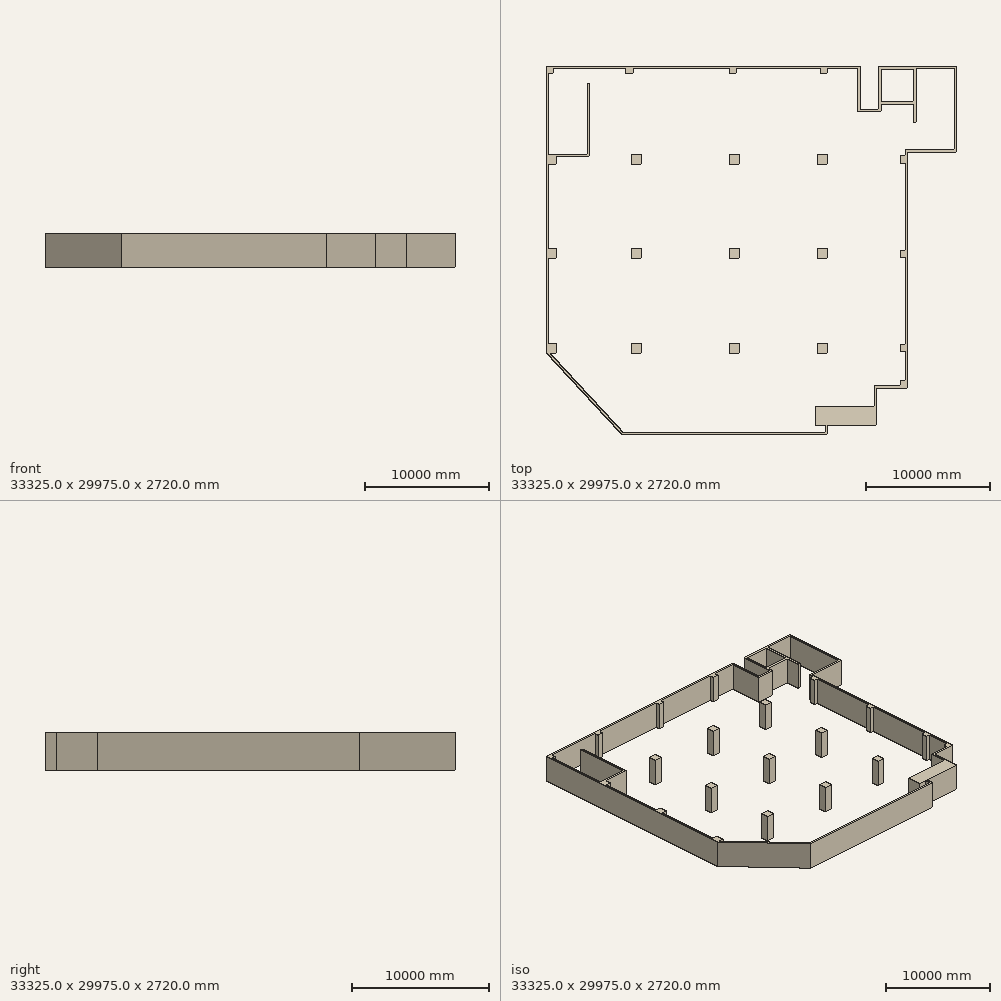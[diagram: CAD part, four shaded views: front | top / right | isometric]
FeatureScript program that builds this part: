
annotation { "Feature Type Name" : "Feature", "Feature Type Description" : "" }
export const myFeature = defineFeature(function(context is Context, id is Id, definition is map)
    precondition{}
    {
        {
            assignVariable(context, id + "F0", {"name" : "Wall_Height", "anyValue" : 2720});
        }
        {
            var Q0;
            Q0=qCreatedBy(makeId("Top.planeOp"),FACE);
            var sketch = newSketch(context, id + "F1", { "sketchPlane" : qUnion([Q0])});
            skLineSegment(sketch, "E0.bottom", {"start": v(0, 0) * mm, "end": v(33325, 0) * mm});
            skLineSegment(sketch, "E0.top", {"start": v(6150, -29975) * mm, "end": v(22850, -29975) * mm});
            skLineSegment(sketch, "E0.left", {"start": v(0, 0) * mm, "end": v(0, -23325) * mm});
            skLineSegment(sketch, "E0.right", {"start": v(33325, 0) * mm, "end": v(33325, -7000) * mm});
            skLineSegment(sketch, "E1", {"start": v(33325, -7000) * mm, "end": v(29350, -7000) * mm});
            skLineSegment(sketch, "E2", {"start": v(29350, -7000) * mm, "end": v(29350, -26190) * mm});
            skLineSegment(sketch, "E3", {"start": v(29350, -26190) * mm, "end": v(26850, -26190) * mm});
            skLineSegment(sketch, "E4", {"start": v(26850, -26190) * mm, "end": v(26850, -29190) * mm});
            skLineSegment(sketch, "E5", {"start": v(26850, -29190) * mm, "end": v(21850, -29190) * mm});
            skLineSegment(sketch, "E6", {"start": v(22850, -29190) * mm, "end": v(22850, -29975) * mm});
            skLineSegment(sketch, "E7", {"start": v(0, -23325) * mm, "end": v(6150, -29975) * mm});
            skLineSegment(sketch, "E8.1", {"start": v(22650, -29190) * mm, "end": v(22650, -29775) * mm});
            skLineSegment(sketch, "E8.2", {"start": v(6237.45, -29775) * mm, "end": v(22650, -29775) * mm});
            skLineSegment(sketch, "E8.3", {"start": v(200, -23246.7) * mm, "end": v(6237.45, -29775) * mm});
            skLineSegment(sketch, "E8.4", {"start": v(200, -600) * mm, "end": v(200, -7175) * mm});
            skLineSegment(sketch, "E8.5", {"start": v(26650, -25990) * mm, "end": v(26650, -27690) * mm});
            skLineSegment(sketch, "E8.6", {"start": v(28750, -25990) * mm, "end": v(26650, -25990) * mm});
            skLineSegment(sketch, "E8.7", {"start": v(29150, -6800) * mm, "end": v(29150, -7300) * mm});
            skLineSegment(sketch, "E8.8", {"start": v(33125, -6800) * mm, "end": v(29150, -6800) * mm});
            skLineSegment(sketch, "E8.9", {"start": v(33125, -200) * mm, "end": v(33125, -6800) * mm});
            skLineSegment(sketch, "E8.10", {"start": v(600, -200) * mm, "end": v(6450, -200) * mm});
            skLineSegment(sketch, "E9.bottom", {"start": v(600, -600) * mm, "end": v(0, -600) * mm});
            skLineSegment(sketch, "E9.left", {"start": v(600, -600) * mm, "end": v(600, 0) * mm});
            skLineSegment(sketch, "E10", {"start": v(7050, 0) * mm, "end": v(7050, -600) * mm});
            skLineSegment(sketch, "E11", {"start": v(6450, -600) * mm, "end": v(7050, -600) * mm});
            skLineSegment(sketch, "E12", {"start": v(6450, -600) * mm, "end": v(6450, 0) * mm});
            skLineSegment(sketch, "E13", {"start": v(14850, 0) * mm, "end": v(14850, -600) * mm});
            skLineSegment(sketch, "E14", {"start": v(14850, -600) * mm, "end": v(15450, -600) * mm});
            skLineSegment(sketch, "E15", {"start": v(15450, -600) * mm, "end": v(15450, 0) * mm});
            skLineSegment(sketch, "E16", {"start": v(22850, 0) * mm, "end": v(22850, -600) * mm});
            skLineSegment(sketch, "E17", {"start": v(22250, -600) * mm, "end": v(22850, -600) * mm});
            skLineSegment(sketch, "E18", {"start": v(22250, -600) * mm, "end": v(22250, 0) * mm});
            skLineSegment(sketch, "E19", {"start": v(0, -23325) * mm, "end": v(800, -23325) * mm});
            skLineSegment(sketch, "E20", {"start": v(800, -23325) * mm, "end": v(800, -22525) * mm});
            skLineSegment(sketch, "E21", {"start": v(800, -22525) * mm, "end": v(0, -22525) * mm});
            skLineSegment(sketch, "E22", {"start": v(0, -15625) * mm, "end": v(800, -15625) * mm});
            skLineSegment(sketch, "E23", {"start": v(800, -15625) * mm, "end": v(800, -14825) * mm});
            skLineSegment(sketch, "E24", {"start": v(800, -14825) * mm, "end": v(0, -14825) * mm});
            skLineSegment(sketch, "E25", {"start": v(0, -7975) * mm, "end": v(800, -7975) * mm});
            skLineSegment(sketch, "E26", {"start": v(800, -7975) * mm, "end": v(800, -7175) * mm});
            skLineSegment(sketch, "E27", {"start": v(800, -7175) * mm, "end": v(0, -7175) * mm});
            skLineSegment(sketch, "E28.bottom", {"start": v(6925, -7975) * mm, "end": v(7725, -7975) * mm});
            skLineSegment(sketch, "E28.top", {"start": v(6925, -7175) * mm, "end": v(7725, -7175) * mm});
            skLineSegment(sketch, "E28.left", {"start": v(6925, -7975) * mm, "end": v(6925, -7175) * mm});
            skLineSegment(sketch, "E28.right", {"start": v(7725, -7975) * mm, "end": v(7725, -7175) * mm});
            skLineSegment(sketch, "E29.bottom", {"start": v(6925, -15625) * mm, "end": v(7725, -15625) * mm});
            skLineSegment(sketch, "E29.top", {"start": v(6925, -14825) * mm, "end": v(7725, -14825) * mm});
            skLineSegment(sketch, "E29.left", {"start": v(6925, -15625) * mm, "end": v(6925, -14825) * mm});
            skLineSegment(sketch, "E29.right", {"start": v(7725, -15625) * mm, "end": v(7725, -14825) * mm});
            skLineSegment(sketch, "E30.bottom", {"start": v(6925, -23325) * mm, "end": v(7725, -23325) * mm});
            skLineSegment(sketch, "E30.top", {"start": v(6925, -22525) * mm, "end": v(7725, -22525) * mm});
            skLineSegment(sketch, "E30.left", {"start": v(6925, -23325) * mm, "end": v(6925, -22525) * mm});
            skLineSegment(sketch, "E30.right", {"start": v(7725, -23325) * mm, "end": v(7725, -22525) * mm});
            skLineSegment(sketch, "E31.1.0.0", {"start": v(15650, -15625) * mm, "end": v(15650, -14825) * mm});
            skLineSegment(sketch, "E31.1.0.1", {"start": v(14850, -23325) * mm, "end": v(15650, -23325) * mm});
            skLineSegment(sketch, "E31.1.0.2", {"start": v(14850, -15625) * mm, "end": v(14850, -14825) * mm});
            skLineSegment(sketch, "E31.1.0.3", {"start": v(14850, -14825) * mm, "end": v(15650, -14825) * mm});
            skLineSegment(sketch, "E31.1.0.4", {"start": v(14850, -22525) * mm, "end": v(15650, -22525) * mm});
            skLineSegment(sketch, "E31.1.0.5", {"start": v(14850, -23325) * mm, "end": v(14850, -22525) * mm});
            skLineSegment(sketch, "E31.1.0.6", {"start": v(15650, -23325) * mm, "end": v(15650, -22525) * mm});
            skLineSegment(sketch, "E31.1.0.7", {"start": v(14850, -15625) * mm, "end": v(15650, -15625) * mm});
            skLineSegment(sketch, "E31.1.0.8", {"start": v(15650, -7975) * mm, "end": v(15650, -7175) * mm});
            skLineSegment(sketch, "E31.1.0.9", {"start": v(14850, -7175) * mm, "end": v(15650, -7175) * mm});
            skLineSegment(sketch, "E31.1.0.10", {"start": v(14850, -7975) * mm, "end": v(14850, -7175) * mm});
            skLineSegment(sketch, "E31.1.0.11", {"start": v(14850, -7975) * mm, "end": v(15650, -7975) * mm});
            skLineSegment(sketch, "E31.direction1", {"start": v(6925, -23325) * mm, "end": v(14850, -23325) * mm, "construction": true});
            skLineSegment(sketch, "E32.1.0.0", {"start": v(22000, -23325) * mm, "end": v(22800, -23325) * mm});
            skLineSegment(sketch, "E32.1.0.1", {"start": v(22000, -7975) * mm, "end": v(22800, -7975) * mm});
            skLineSegment(sketch, "E32.1.0.2", {"start": v(22800, -23325) * mm, "end": v(22800, -22525) * mm});
            skLineSegment(sketch, "E32.1.0.3", {"start": v(22000, -7175) * mm, "end": v(22800, -7175) * mm});
            skLineSegment(sketch, "E32.1.0.4", {"start": v(22000, -7975) * mm, "end": v(22000, -7175) * mm});
            skLineSegment(sketch, "E32.1.0.5", {"start": v(22800, -15625) * mm, "end": v(22800, -14825) * mm});
            skLineSegment(sketch, "E32.1.0.6", {"start": v(22800, -7975) * mm, "end": v(22800, -7175) * mm});
            skLineSegment(sketch, "E32.1.0.7", {"start": v(22000, -15625) * mm, "end": v(22800, -15625) * mm});
            skLineSegment(sketch, "E32.1.0.8", {"start": v(22000, -14825) * mm, "end": v(22800, -14825) * mm});
            skLineSegment(sketch, "E32.1.0.9", {"start": v(22000, -22525) * mm, "end": v(22800, -22525) * mm});
            skLineSegment(sketch, "E32.1.0.10", {"start": v(22000, -23325) * mm, "end": v(22000, -22525) * mm});
            skLineSegment(sketch, "E32.1.0.11", {"start": v(22000, -15625) * mm, "end": v(22000, -14825) * mm});
            skLineSegment(sketch, "E32.direction1", {"start": v(6925, -23325) * mm, "end": v(22000, -23325) * mm, "construction": true});
            skLineSegment(sketch, "E33.trimOffspring", {"start": v(7050, -200) * mm, "end": v(14850, -200) * mm});
            skLineSegment(sketch, "E34.trimOffspring", {"start": v(15450, -200) * mm, "end": v(22250, -200) * mm});
            skLineSegment(sketch, "E35.trimOffspring", {"start": v(22850, -200) * mm, "end": v(25300, -200) * mm});
            skLineSegment(sketch, "E36.trimOffspring", {"start": v(200, -7975) * mm, "end": v(200, -14825) * mm});
            skLineSegment(sketch, "E37.trimOffspring", {"start": v(200, -15625) * mm, "end": v(200, -22525) * mm});
            skLineSegment(sketch, "E38", {"start": v(26850, -27690) * mm, "end": v(21850, -27690) * mm});
            skLineSegment(sketch, "E39", {"start": v(21850, -27690) * mm, "end": v(21850, -29190) * mm});
            skLineSegment(sketch, "E40", {"start": v(29350, -25590) * mm, "end": v(28750, -25590) * mm});
            skLineSegment(sketch, "E41", {"start": v(28750, -25590) * mm, "end": v(28750, -26190) * mm});
            skLineSegment(sketch, "E42", {"start": v(29350, -7900) * mm, "end": v(28750, -7900) * mm});
            skLineSegment(sketch, "E43", {"start": v(28750, -7900) * mm, "end": v(28750, -7300) * mm});
            skLineSegment(sketch, "E44", {"start": v(28750, -7300) * mm, "end": v(29350, -7300) * mm});
            skLineSegment(sketch, "E45", {"start": v(29350, -23200) * mm, "end": v(28750, -23200) * mm});
            skLineSegment(sketch, "E46", {"start": v(28750, -23200) * mm, "end": v(28750, -22600) * mm});
            skLineSegment(sketch, "E47", {"start": v(28750, -22600) * mm, "end": v(29350, -22600) * mm});
            skLineSegment(sketch, "E48", {"start": v(29350, -15550) * mm, "end": v(28750, -15550) * mm});
            skLineSegment(sketch, "E49", {"start": v(28750, -15550) * mm, "end": v(28750, -14950) * mm});
            skLineSegment(sketch, "E50", {"start": v(28750, -14950) * mm, "end": v(29350, -14950) * mm});
            skLineSegment(sketch, "E51.trimOffspring", {"start": v(29150, -7900) * mm, "end": v(29150, -14950) * mm});
            skLineSegment(sketch, "E52.trimOffspring", {"start": v(29150, -15550) * mm, "end": v(29150, -22600) * mm});
            skLineSegment(sketch, "E53.trimOffspring", {"start": v(29150, -23200) * mm, "end": v(29150, -25590) * mm});
            skLineSegment(sketch, "E54", {"start": v(800, -7175) * mm, "end": v(3300, -7175) * mm});
            skLineSegment(sketch, "E55", {"start": v(3300, -7175) * mm, "end": v(3300, -1400) * mm});
            skLineSegment(sketch, "E56", {"start": v(3300, -1400) * mm, "end": v(3500, -1400) * mm});
            skLineSegment(sketch, "E57", {"start": v(3500, -1400) * mm, "end": v(3500, -7375) * mm});
            skLineSegment(sketch, "E58", {"start": v(3500, -7375) * mm, "end": v(800, -7375) * mm});
            skLineSegment(sketch, "E59", {"start": v(29150, -25590) * mm, "end": v(29150, -25990) * mm});
            skLineSegment(sketch, "E60", {"start": v(29150, -25990) * mm, "end": v(28750, -25990) * mm});
            skLineSegment(sketch, "E61", {"start": v(29150, -23200) * mm, "end": v(29150, -22600) * mm});
            skLineSegment(sketch, "E62", {"start": v(29150, -15550) * mm, "end": v(29150, -14950) * mm});
            skLineSegment(sketch, "E63", {"start": v(29150, -7300) * mm, "end": v(29150, -7900) * mm});
            skLineSegment(sketch, "E64", {"start": v(22850, -200) * mm, "end": v(22250, -200) * mm});
            skLineSegment(sketch, "E65", {"start": v(15450, -200) * mm, "end": v(14850, -200) * mm});
            skLineSegment(sketch, "E66", {"start": v(7050, -200) * mm, "end": v(6450, -200) * mm});
            skLineSegment(sketch, "E67", {"start": v(600, -200) * mm, "end": v(200, -200) * mm});
            skLineSegment(sketch, "E68", {"start": v(200, -200) * mm, "end": v(200, -600) * mm});
            skLineSegment(sketch, "E69", {"start": v(200, -7175) * mm, "end": v(200, -7975) * mm});
            skLineSegment(sketch, "E70", {"start": v(200, -14825) * mm, "end": v(200, -15625) * mm});
            skLineSegment(sketch, "E71", {"start": v(200, -22525) * mm, "end": v(200, -23246.7) * mm});
            skLineSegment(sketch, "E72", {"start": v(30100, -200) * mm, "end": v(30100, -4550) * mm});
            skLineSegment(sketch, "E73", {"start": v(30100, -4550) * mm, "end": v(29850, -4550) * mm});
            skLineSegment(sketch, "E74", {"start": v(29850, -4550) * mm, "end": v(29850, -3100) * mm});
            skLineSegment(sketch, "E75", {"start": v(29850, -3100) * mm, "end": v(27200, -3100) * mm});
            skLineSegment(sketch, "E76", {"start": v(27200, -3100) * mm, "end": v(27200, -3725) * mm});
            skLineSegment(sketch, "E77", {"start": v(27200, -3725) * mm, "end": v(25300, -3725) * mm});
            skLineSegment(sketch, "E78", {"start": v(25300, -3725) * mm, "end": v(25300, -200) * mm});
            skLineSegment(sketch, "E79", {"start": v(25500, 0) * mm, "end": v(25500, -3525) * mm});
            skLineSegment(sketch, "E80", {"start": v(25500, -3525) * mm, "end": v(27000, -3525) * mm});
            skLineSegment(sketch, "E81", {"start": v(27000, -3525) * mm, "end": v(27000, 0) * mm});
            skLineSegment(sketch, "E82.trimOffspring", {"start": v(30100, -200) * mm, "end": v(33125, -200) * mm});
            skLineSegment(sketch, "E83.bottom", {"start": v(27250, -250) * mm, "end": v(29850, -250) * mm});
            skLineSegment(sketch, "E83.top", {"start": v(27250, -2850) * mm, "end": v(29850, -2850) * mm});
            skLineSegment(sketch, "E83.left", {"start": v(27250, -250) * mm, "end": v(27250, -2850) * mm});
            skLineSegment(sketch, "E83.right", {"start": v(29850, -250) * mm, "end": v(29850, -2850) * mm});
            skLineSegment(sketch, "E84.bottom", {"start": v(1900, -5875) * mm, "end": v(2100, -5875) * mm});
            skLineSegment(sketch, "E84.top", {"start": v(1900, -3175) * mm, "end": v(2100, -3175) * mm});
            skLineSegment(sketch, "E84.left", {"start": v(1900, -5875) * mm, "end": v(1900, -3175) * mm});
            skLineSegment(sketch, "E84.right", {"start": v(2100, -5875) * mm, "end": v(2100, -3175) * mm});
            skSolve(sketch);
        }
        {
            var Q0;
            Q0=makeQuery(id+"F1.imprint","IMPRINT",FACE,{"disambiguationData":[TD([[makeQuery(id+"F1.imprint","IMPRINT",EDGE,{"derivedFrom":sQuery(id+"F1.wireOp",EDGE,"E0.top")}),1.0]])]});
            var Q1;
            {var subQ3=sQuery(id+"F1.wireOp",EDGE,"E71");Q1=makeQuery(id+"F1.imprint","IMPRINT",FACE,{"disambiguationData":[TD([[makeQuery(id+"F1.imprint","IMPRINT",EDGE,{"derivedFrom":subQ3}),-1.0]])]});}
            var Q2;
            {var subQ1=sQuery(id+"F1.wireOp",EDGE,"E20");Q2=makeQuery(id+"F1.imprint","IMPRINT",FACE,{"disambiguationData":[TD([[makeQuery(id+"F1.imprint","IMPRINT",EDGE,{"derivedFrom":subQ1}),1.0]])]});}
            var Q3;
            {var subQ48=sQuery(id+"F1.wireOp",EDGE,"E8.1");Q3=makeQuery(id+"F1.imprint","IMPRINT",FACE,{"disambiguationData":[TD([[makeQuery(id+"F1.imprint","IMPRINT",EDGE,{"derivedFrom":subQ48}),-1.0]])]});}
            var Q4;
            {var subQ5=sQuery(id+"F1.wireOp",EDGE,"E37.trimOffspring");Q4=makeQuery(id+"F1.imprint","IMPRINT",FACE,{"disambiguationData":[TD([[makeQuery(id+"F1.imprint","IMPRINT",EDGE,{"derivedFrom":subQ5}),-1.0]])]});}
            var Q5;
            {var subQ0=sQuery(id+"F1.wireOp",EDGE,"E23");Q5=makeQuery(id+"F1.imprint","IMPRINT",FACE,{"disambiguationData":[TD([[makeQuery(id+"F1.imprint","IMPRINT",EDGE,{"derivedFrom":subQ0}),1.0]])]});}
            var Q6;
            {var subQ5=sQuery(id+"F1.wireOp",EDGE,"E70");Q6=makeQuery(id+"F1.imprint","IMPRINT",FACE,{"disambiguationData":[TD([[makeQuery(id+"F1.imprint","IMPRINT",EDGE,{"derivedFrom":subQ5}),-1.0]])]});}
            var Q7;
            {var subQ5=sQuery(id+"F1.wireOp",EDGE,"E36.trimOffspring");Q7=makeQuery(id+"F1.imprint","IMPRINT",FACE,{"disambiguationData":[TD([[makeQuery(id+"F1.imprint","IMPRINT",EDGE,{"derivedFrom":subQ5}),-1.0]])]});}
            var Q8;
            Q8=makeQuery(id+"F1.imprint","IMPRINT",FACE,{"disambiguationData":[TD([[makeQuery(id+"F1.imprint","IMPRINT",EDGE,{"derivedFrom":sQuery(id+"F1.wireOp",EDGE,"E29.bottom")}),1.0]])]});
            var Q9;
            {var subQ0=sQuery(id+"F1.wireOp",EDGE,"E54");Q9=makeQuery(id+"F1.imprint","IMPRINT",FACE,{"disambiguationData":[TD([[makeQuery(id+"F1.imprint","IMPRINT",EDGE,{"derivedFrom":subQ0}),-1.0]])]});}
            var Q10;
            {var subQ0=sQuery(id+"F1.wireOp",EDGE,"E69");Q10=makeQuery(id+"F1.imprint","IMPRINT",FACE,{"disambiguationData":[TD([[makeQuery(id+"F1.imprint","IMPRINT",EDGE,{"derivedFrom":subQ0}),1.0]])]});}
            var Q11;
            {var subQ5=sQuery(id+"F1.wireOp",EDGE,"E69");Q11=makeQuery(id+"F1.imprint","IMPRINT",FACE,{"disambiguationData":[TD([[makeQuery(id+"F1.imprint","IMPRINT",EDGE,{"derivedFrom":subQ5}),-1.0]])]});}
            var Q12;
            Q12=makeQuery(id+"F1.imprint","IMPRINT",FACE,{"disambiguationData":[TD([[makeQuery(id+"F1.imprint","IMPRINT",EDGE,{"derivedFrom":sQuery(id+"F1.wireOp",EDGE,"E84.bottom")}),1.0]])]});
            var Q13;
            {var subQ4=sQuery(id+"F1.wireOp",EDGE,"E67");Q13=makeQuery(id+"F1.imprint","IMPRINT",FACE,{"disambiguationData":[TD([[makeQuery(id+"F1.imprint","IMPRINT",EDGE,{"derivedFrom":subQ4}),1.0]])]});}
            var Q14;
            {var subQ4=sQuery(id+"F1.wireOp",EDGE,"E67");Q14=makeQuery(id+"F1.imprint","IMPRINT",FACE,{"disambiguationData":[TD([[makeQuery(id+"F1.imprint","IMPRINT",EDGE,{"derivedFrom":subQ4}),-1.0]])]});}
            var Q15;
            {var subQ5=sQuery(id+"F1.wireOp",EDGE,"E8.10");Q15=makeQuery(id+"F1.imprint","IMPRINT",FACE,{"disambiguationData":[TD([[makeQuery(id+"F1.imprint","IMPRINT",EDGE,{"derivedFrom":subQ5}),1.0]])]});}
            var Q16;
            {var subQ0=sQuery(id+"F1.wireOp",EDGE,"E11");Q16=makeQuery(id+"F1.imprint","IMPRINT",FACE,{"disambiguationData":[TD([[makeQuery(id+"F1.imprint","IMPRINT",EDGE,{"derivedFrom":subQ0}),1.0]])]});}
            var Q17;
            {var subQ5=sQuery(id+"F1.wireOp",EDGE,"E66");Q17=makeQuery(id+"F1.imprint","IMPRINT",FACE,{"disambiguationData":[TD([[makeQuery(id+"F1.imprint","IMPRINT",EDGE,{"derivedFrom":subQ5}),-1.0]])]});}
            var Q18;
            {var subQ5=sQuery(id+"F1.wireOp",EDGE,"E33.trimOffspring");Q18=makeQuery(id+"F1.imprint","IMPRINT",FACE,{"disambiguationData":[TD([[makeQuery(id+"F1.imprint","IMPRINT",EDGE,{"derivedFrom":subQ5}),1.0]])]});}
            var Q19;
            {var subQ0=sQuery(id+"F1.wireOp",EDGE,"E14");Q19=makeQuery(id+"F1.imprint","IMPRINT",FACE,{"disambiguationData":[TD([[makeQuery(id+"F1.imprint","IMPRINT",EDGE,{"derivedFrom":subQ0}),1.0]])]});}
            var Q20;
            {var subQ5=sQuery(id+"F1.wireOp",EDGE,"E65");Q20=makeQuery(id+"F1.imprint","IMPRINT",FACE,{"disambiguationData":[TD([[makeQuery(id+"F1.imprint","IMPRINT",EDGE,{"derivedFrom":subQ5}),-1.0]])]});}
            var Q21;
            {var subQ5=sQuery(id+"F1.wireOp",EDGE,"E34.trimOffspring");Q21=makeQuery(id+"F1.imprint","IMPRINT",FACE,{"disambiguationData":[TD([[makeQuery(id+"F1.imprint","IMPRINT",EDGE,{"derivedFrom":subQ5}),1.0]])]});}
            var Q22;
            Q22=makeQuery(id+"F1.imprint","IMPRINT",FACE,{"disambiguationData":[TD([[makeQuery(id+"F1.imprint","IMPRINT",EDGE,{"derivedFrom":sQuery(id+"F1.wireOp",EDGE,"E28.bottom")}),1.0]])]});
            var Q23;
            Q23=makeQuery(id+"F1.imprint","IMPRINT",FACE,{"disambiguationData":[TD([[makeQuery(id+"F1.imprint","IMPRINT",EDGE,{"derivedFrom":sQuery(id+"F1.wireOp",EDGE,"E31.1.0.8")}),1.0]])]});
            var Q24;
            Q24=makeQuery(id+"F1.imprint","IMPRINT",FACE,{"disambiguationData":[TD([[makeQuery(id+"F1.imprint","IMPRINT",EDGE,{"derivedFrom":sQuery(id+"F1.wireOp",EDGE,"E32.1.0.1")}),1.0]])]});
            var Q25;
            {var subQ0=sQuery(id+"F1.wireOp",EDGE,"E17");Q25=makeQuery(id+"F1.imprint","IMPRINT",FACE,{"disambiguationData":[TD([[makeQuery(id+"F1.imprint","IMPRINT",EDGE,{"derivedFrom":subQ0}),1.0]])]});}
            var Q26;
            {var subQ5=sQuery(id+"F1.wireOp",EDGE,"E64");Q26=makeQuery(id+"F1.imprint","IMPRINT",FACE,{"disambiguationData":[TD([[makeQuery(id+"F1.imprint","IMPRINT",EDGE,{"derivedFrom":subQ5}),-1.0]])]});}
            var Q27;
            {var subQ2=sQuery(id+"F1.wireOp",EDGE,"E0.right");Q27=makeQuery(id+"F1.imprint","IMPRINT",FACE,{"disambiguationData":[TD([[makeQuery(id+"F1.imprint","IMPRINT",EDGE,{"derivedFrom":subQ2}),-1.0]])]});}
            var Q28;
            {var subQ0=sQuery(id+"F1.wireOp",EDGE,"E43");Q28=makeQuery(id+"F1.imprint","IMPRINT",FACE,{"disambiguationData":[TD([[makeQuery(id+"F1.imprint","IMPRINT",EDGE,{"derivedFrom":subQ0}),-1.0]])]});}
            var Q29;
            {var subQ5=sQuery(id+"F1.wireOp",EDGE,"E63");Q29=makeQuery(id+"F1.imprint","IMPRINT",FACE,{"disambiguationData":[TD([[makeQuery(id+"F1.imprint","IMPRINT",EDGE,{"derivedFrom":subQ5}),1.0]])]});}
            var Q30;
            {var subQ5=sQuery(id+"F1.wireOp",EDGE,"E51.trimOffspring");Q30=makeQuery(id+"F1.imprint","IMPRINT",FACE,{"disambiguationData":[TD([[makeQuery(id+"F1.imprint","IMPRINT",EDGE,{"derivedFrom":subQ5}),1.0]])]});}
            var Q31;
            {var subQ0=sQuery(id+"F1.wireOp",EDGE,"E49");Q31=makeQuery(id+"F1.imprint","IMPRINT",FACE,{"disambiguationData":[TD([[makeQuery(id+"F1.imprint","IMPRINT",EDGE,{"derivedFrom":subQ0}),-1.0]])]});}
            var Q32;
            {var subQ5=sQuery(id+"F1.wireOp",EDGE,"E52.trimOffspring");Q32=makeQuery(id+"F1.imprint","IMPRINT",FACE,{"disambiguationData":[TD([[makeQuery(id+"F1.imprint","IMPRINT",EDGE,{"derivedFrom":subQ5}),1.0]])]});}
            var Q33;
            {var subQ5=sQuery(id+"F1.wireOp",EDGE,"E62");Q33=makeQuery(id+"F1.imprint","IMPRINT",FACE,{"disambiguationData":[TD([[makeQuery(id+"F1.imprint","IMPRINT",EDGE,{"derivedFrom":subQ5}),-1.0]])]});}
            var Q34;
            {var subQ0=sQuery(id+"F1.wireOp",EDGE,"E46");Q34=makeQuery(id+"F1.imprint","IMPRINT",FACE,{"disambiguationData":[TD([[makeQuery(id+"F1.imprint","IMPRINT",EDGE,{"derivedFrom":subQ0}),-1.0]])]});}
            var Q35;
            {var subQ5=sQuery(id+"F1.wireOp",EDGE,"E61");Q35=makeQuery(id+"F1.imprint","IMPRINT",FACE,{"disambiguationData":[TD([[makeQuery(id+"F1.imprint","IMPRINT",EDGE,{"derivedFrom":subQ5}),-1.0]])]});}
            var Q36;
            {var subQ5=sQuery(id+"F1.wireOp",EDGE,"E53.trimOffspring");Q36=makeQuery(id+"F1.imprint","IMPRINT",FACE,{"disambiguationData":[TD([[makeQuery(id+"F1.imprint","IMPRINT",EDGE,{"derivedFrom":subQ5}),1.0]])]});}
            var Q37;
            {var subQ3=sQuery(id+"F1.wireOp",EDGE,"E59");Q37=makeQuery(id+"F1.imprint","IMPRINT",FACE,{"disambiguationData":[TD([[makeQuery(id+"F1.imprint","IMPRINT",EDGE,{"derivedFrom":subQ3}),-1.0]])]});}
            var Q38;
            {var subQ8=sQuery(id+"F1.wireOp",EDGE,"E59");Q38=makeQuery(id+"F1.imprint","IMPRINT",FACE,{"disambiguationData":[TD([[makeQuery(id+"F1.imprint","IMPRINT",EDGE,{"derivedFrom":subQ8}),1.0]])]});}
            var Q39;
            {var subQ1=sQuery(id+"F1.wireOp",EDGE,"E8.5");Q39=makeQuery(id+"F1.imprint","IMPRINT",FACE,{"disambiguationData":[TD([[makeQuery(id+"F1.imprint","IMPRINT",EDGE,{"derivedFrom":subQ1}),1.0]])]});}
            var Q40;
            {var subQ0=sQuery(id+"F1.wireOp",EDGE,"E39");Q40=makeQuery(id+"F1.imprint","IMPRINT",FACE,{"disambiguationData":[TD([[makeQuery(id+"F1.imprint","IMPRINT",EDGE,{"derivedFrom":subQ0}),1.0]])]});}
            var Q41;
            Q41=makeQuery(id+"F1.imprint","IMPRINT",FACE,{"disambiguationData":[TD([[makeQuery(id+"F1.imprint","IMPRINT",EDGE,{"derivedFrom":sQuery(id+"F1.wireOp",EDGE,"E32.1.0.0")}),1.0]])]});
            var Q42;
            Q42=makeQuery(id+"F1.imprint","IMPRINT",FACE,{"disambiguationData":[TD([[makeQuery(id+"F1.imprint","IMPRINT",EDGE,{"derivedFrom":sQuery(id+"F1.wireOp",EDGE,"E31.1.0.1")}),1.0]])]});
            var Q43;
            Q43=makeQuery(id+"F1.imprint","IMPRINT",FACE,{"disambiguationData":[TD([[makeQuery(id+"F1.imprint","IMPRINT",EDGE,{"derivedFrom":sQuery(id+"F1.wireOp",EDGE,"E30.bottom")}),1.0]])]});
            var Q44;
            Q44=makeQuery(id+"F1.imprint","IMPRINT",FACE,{"disambiguationData":[TD([[makeQuery(id+"F1.imprint","IMPRINT",EDGE,{"derivedFrom":sQuery(id+"F1.wireOp",EDGE,"E31.1.0.0")}),1.0]])]});
            var Q45;
            Q45=makeQuery(id+"F1.imprint","IMPRINT",FACE,{"disambiguationData":[TD([[makeQuery(id+"F1.imprint","IMPRINT",EDGE,{"derivedFrom":sQuery(id+"F1.wireOp",EDGE,"E32.1.0.5")}),1.0]])]});
            var Q46;
            {var subQ5=sQuery(id+"F1.wireOp",EDGE,"E8.4");Q46=makeQuery(id+"F1.imprint","IMPRINT",FACE,{"disambiguationData":[TD([[makeQuery(id+"F1.imprint","IMPRINT",EDGE,{"derivedFrom":subQ5}),-1.0]])]});}
            extrude(context, id + "F2", {"entities" : qUnion([Q0, Q1, Q2, Q3, Q4, Q5, Q6, Q7, Q8, Q9, Q10, Q11, Q12, Q13, Q14, Q15, Q16, Q17, Q18, Q19, Q20, Q21, Q22, Q23, Q24, Q25, Q26, Q27, Q28, Q29, Q30, Q31, Q32, Q33, Q34, Q35, Q36, Q37, Q38, Q39, Q40, Q41, Q42, Q43, Q44, Q45, Q46]), "depth" : (getVariable(context, 'Wall_Height')) * mm, "offsetDistance" : 25 * mm});
        }
        {
            var Q0;
            {var subQ48=sQuery(id+"F1.wireOp",EDGE,"E8.1");Q0=makeQuery(id+"F1.imprint","IMPRINT",FACE,{"disambiguationData":[TD([[makeQuery(id+"F1.imprint","IMPRINT",EDGE,{"derivedFrom":subQ48}),-1.0]])]});}
            var Q1;
            Q1=makeQuery(id+"F1.imprint","IMPRINT",FACE,{"disambiguationData":[TD([[makeQuery(id+"F1.imprint","IMPRINT",EDGE,{"derivedFrom":sQuery(id+"F1.wireOp",EDGE,"E84.bottom")}),1.0]])]});
            var Q2;
            Q2=makeQuery(id+"F2.opExtrude","SWEPT_BODY",BODY,{"disambiguationData":[OSD([sQuery(id+"F1.wireOp",EDGE,"E0.bottom"),sQuery(id+"F1.wireOp",EDGE,"E0.top"),sQuery(id+"F1.wireOp",EDGE,"E0.left"),sQuery(id+"F1.wireOp",EDGE,"E0.right"),sQuery(id+"F1.wireOp",EDGE,"E1"),sQuery(id+"F1.wireOp",EDGE,"E2"),sQuery(id+"F1.wireOp",EDGE,"E3"),sQuery(id+"F1.wireOp",EDGE,"E4"),sQuery(id+"F1.wireOp",EDGE,"E5"),sQuery(id+"F1.wireOp",EDGE,"E6"),sQuery(id+"F1.wireOp",EDGE,"E7"),sQuery(id+"F1.wireOp",EDGE,"E79"),sQuery(id+"F1.wireOp",EDGE,"E80"),sQuery(id+"F1.wireOp",EDGE,"E81"),sQuery(id+"F1.wireOp",EDGE,"E83.bottom"),sQuery(id+"F1.wireOp",EDGE,"E83.top"),sQuery(id+"F1.wireOp",EDGE,"E83.left"),sQuery(id+"F1.wireOp",EDGE,"E83.right")])]});
            extrude(context, id + "F3", {"entities" : qUnion([Q0, Q1]), "operationType" : NewBodyOperationType.REMOVE, "endBound" : BoundingType.UP_TO_BODY, "depth" : 25 * mm, "endBoundEntityBody" : qUnion([Q2]), "offsetDistance" : 25 * mm});
        }
    });
